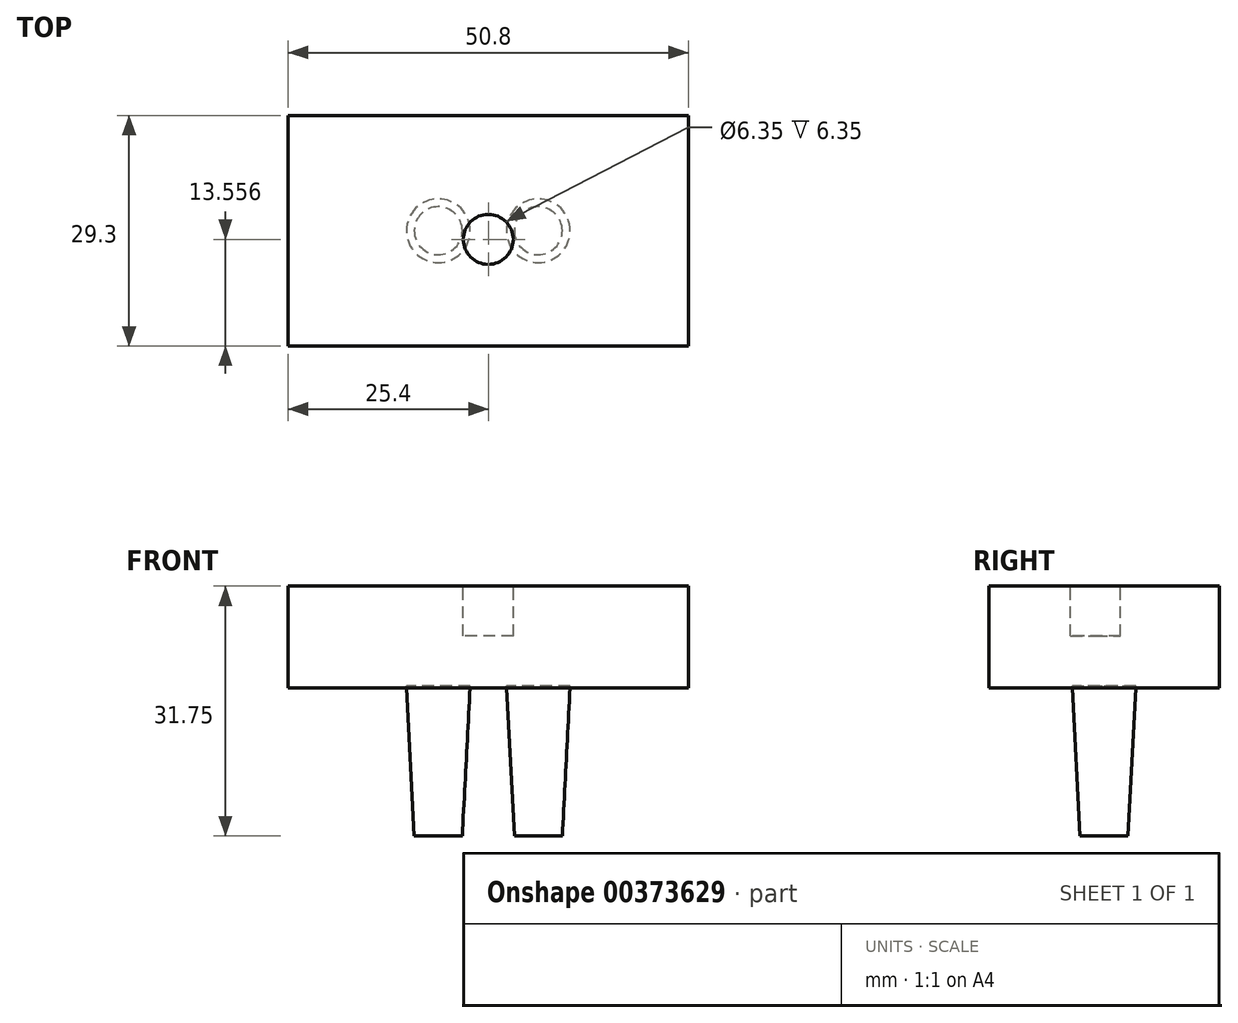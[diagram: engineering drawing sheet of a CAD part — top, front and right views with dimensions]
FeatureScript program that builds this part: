
annotation { "Feature Type Name" : "Feature", "Feature Type Description" : "" }
export const myFeature = defineFeature(function(context is Context, id is Id, definition is map)
    precondition{}
    {
        {
            var Q0;
            Q0=qCreatedBy(makeId("Top.planeOp"),FACE);
            var sketch = newSketch(context, id + "F0", { "sketchPlane" : qUnion([Q0])});
            skCircle(sketch, "E0", {"center": v(6.35, 0) * mm, "radius": 3.05 * mm});
            skCircle(sketch, "E1.MirrorC", {"center": v(-6.35, 0) * mm, "radius": 3.05 * mm});
            skSolve(sketch);
        }
        {
            var Q0;
            Q0 = qSketchRegion(id + "F0", true);
            extrude(context, id + "F1", {"entities" : qUnion([Q0]), "depth" : 19.05 * mm, "hasDraft" : true, "draftAngle" : 3 * degree});
        }
        {
            var Q0;
            Q0=makeQuery(id+"F1.opExtrude","CAP_FACE",FACE,{"disambiguationData":[OSD([sQuery(id+"F0.wireOp",EDGE,"E1.MirrorC")])],"isStart":false});
            var sketch = newSketch(context, id + "F2", { "sketchPlane" : qUnion([Q0])});
            skLineSegment(sketch, "E2.bottom", {"start": v(-25.4, -14.65) * mm, "end": v(25.4, -14.65) * mm});
            skLineSegment(sketch, "E2.top", {"start": v(-25.4, 14.65) * mm, "end": v(25.4, 14.65) * mm});
            skLineSegment(sketch, "E2.left", {"start": v(-25.4, -14.65) * mm, "end": v(-25.4, 14.65) * mm});
            skLineSegment(sketch, "E2.right", {"start": v(25.4, -14.65) * mm, "end": v(25.4, 14.65) * mm});
            skPoint(sketch, "E2.middle", {"position": v(0, 0) * mm});
            skSolve(sketch);
        }
        {
            var Q0;
            Q0 = qSketchRegion(id + "F2", true);
            extrude(context, id + "F3", {"entities" : qUnion([Q0]), "depth" : 12.7 * mm, "hasSecondDirection" : true, "secondDirectionOppositeDirection" : true, "secondDirectionDepth" : 0.25 * mm});
        }
        {
            var Q0;
            Q0=makeQuery(id+"F3.opExtrude","CAP_FACE",FACE,{"disambiguationData":[OSD([sQuery(id+"F2.wireOp",EDGE,"E2.bottom"),sQuery(id+"F2.wireOp",EDGE,"E2.top"),sQuery(id+"F2.wireOp",EDGE,"E2.left"),sQuery(id+"F2.wireOp",EDGE,"E2.right")])],"isStart":false});
            var sketch = newSketch(context, id + "F4", { "sketchPlane" : qUnion([Q0])});
            skCircle(sketch, "E3", {"center": v(0, -1.1) * mm, "radius": 3.18 * mm});
            skSolve(sketch);
        }
        {
            var Q0;
            Q0=makeQuery(id+"F4.imprint","IMPRINT",FACE,{"disambiguationData":[TD([[makeQuery(id+"F4.imprint","IMPRINT",EDGE,{"derivedFrom":sQuery(id+"F4.wireOp",EDGE,"E3")}),1.0]])]});
            extrude(context, id + "F5", {"entities" : qUnion([Q0]), "operationType" : NewBodyOperationType.REMOVE, "oppositeDirection" : true, "depth" : 6.35 * mm});
        }
    });
